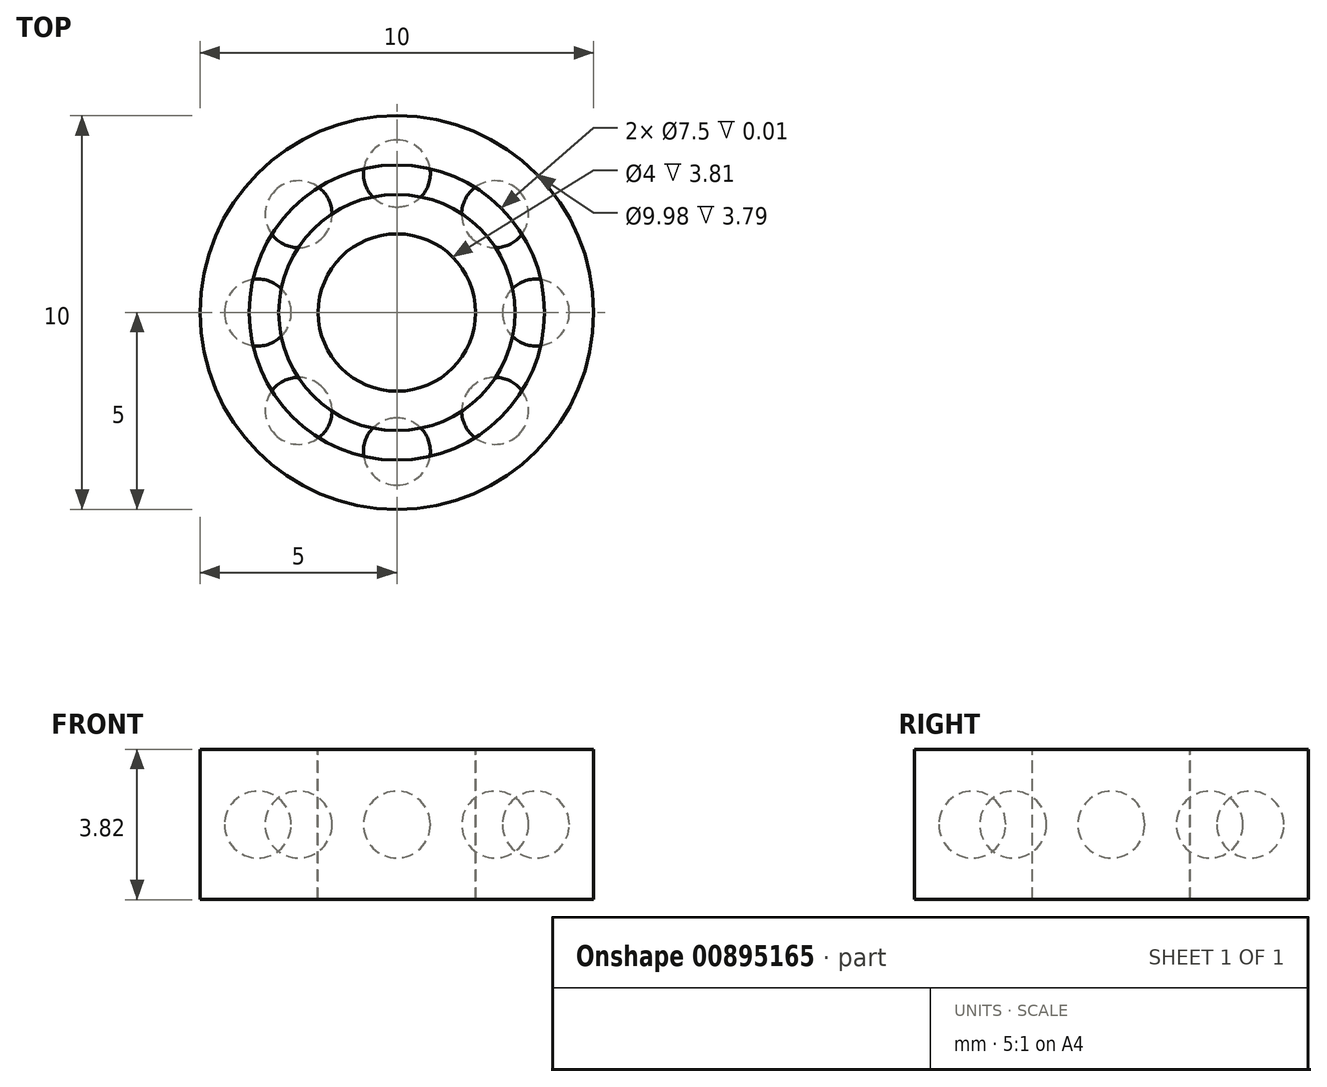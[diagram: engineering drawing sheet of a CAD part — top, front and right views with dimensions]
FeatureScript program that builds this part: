
annotation { "Feature Type Name" : "Feature", "Feature Type Description" : "" }
export const myFeature = defineFeature(function(context is Context, id is Id, definition is map)
    precondition{}
    {
        {
            var Q0;
            Q0=qCreatedBy(makeId("Top.planeOp"),FACE);
            var sketch = newSketch(context, id + "F0", { "sketchPlane" : qUnion([Q0])});
            skCircle(sketch, "E0", {"center": v(0, 0) * mm, "radius": 5 * mm});
            skSolve(sketch);
        }
        {
            var Q0;
            Q0=makeQuery(id+"F0.imprint","IMPRINT",FACE,{"disambiguationData":[TD([[makeQuery(id+"F0.imprint","IMPRINT",EDGE,{"derivedFrom":sQuery(id+"F0.wireOp",EDGE,"E0")}),1.0]])]});
            extrude(context, id + "F1", {"entities" : qUnion([Q0]), "endBound" : BoundingType.SYMMETRIC, "depth" : 3.8 * mm, "offsetDistance" : 25.4 * mm});
        }
        {
            var Q0;
            Q0=makeQuery(id+"F1.opExtrude","CAP_FACE",FACE,{"disambiguationData":[OSD([sQuery(id+"F0.wireOp",EDGE,"E0")])],"isStart":false});
            var sketch = newSketch(context, id + "F2", { "sketchPlane" : qUnion([Q0])});
            skCircle(sketch, "E1", {"center": v(0, 0) * mm, "radius": 2 * mm});
            skSolve(sketch);
        }
        {
            var Q0;
            Q0 = qSketchRegion(id + "F2", true);
            extrude(context, id + "F3", {"entities" : qUnion([Q0]), "operationType" : NewBodyOperationType.REMOVE, "endBound" : BoundingType.SYMMETRIC, "oppositeDirection" : true, "depth" : 25.4 * mm, "offsetDistance" : 25.4 * mm});
        }
        {
            var Q0;
            Q0=makeQuery(id+"F1.opExtrude","CAP_FACE",FACE,{"disambiguationData":[OSD([sQuery(id+"F0.wireOp",EDGE,"E0")])],"isStart":false});
            var sketch = newSketch(context, id + "F4", { "sketchPlane" : qUnion([Q0])});
            skCircle(sketch, "E2", {"center": v(0, 0) * mm, "radius": 3 * mm});
            skCircle(sketch, "E3", {"center": v(0, 0) * mm, "radius": 3.75 * mm});
            skSolve(sketch);
        }
        {
            var Q0;
            Q0=makeQuery(id+"F4.imprint","IMPRINT",FACE,{"disambiguationData":[TD([[makeQuery(id+"F4.imprint","IMPRINT",EDGE,{"derivedFrom":sQuery(id+"F4.wireOp",EDGE,"E2")}),-1.0]])]});
            extrude(context, id + "F5", {"entities" : qUnion([Q0]), "operationType" : NewBodyOperationType.REMOVE, "oppositeDirection" : true, "depth" : 25 * mm, "offsetDistance" : 25 * mm});
        }
        {
            var Q0;
            Q0=makeQuery(id+"F5.boolean.opBoolean","COPY",FACE,{"derivedFrom":makeQuery(id+"F5.opExtrude","SWEPT_FACE",FACE,{"disambiguationData":[OSD([sQuery(id+"F4.wireOp",EDGE,"E2")])]})});
            shell(context, id + "F6", {"entities" : qUnion([Q0]), "thickness" : 0.01 * mm});
        }
        {
            var Q0;
            Q0=makeQuery(id+"F5.boolean.opBoolean","COPY",FACE,{"derivedFrom":makeQuery(id+"F5.opExtrude","SWEPT_FACE",FACE,{"disambiguationData":[OSD([sQuery(id+"F4.wireOp",EDGE,"E3")])]})});
            shell(context, id + "F7", {"entities" : qUnion([Q0]), "thickness" : 0.01 * mm});
        }
        {
            var Q0;
            Q0=qCreatedBy(makeId("Top.planeOp"),FACE);
            var sketch = newSketch(context, id + "F8", { "sketchPlane" : qUnion([Q0])});
            skCircle(sketch, "E4", {"center": v(3.53, 0) * mm, "radius": 0.85 * mm});
            skLineSegment(sketch, "E5", {"start": v(4.38, 0) * mm, "end": v(2.68, 0) * mm});
            skSolve(sketch);
        }
        {
            var Q0;
            {var subQ0=sQuery(id+"F8.wireOp",EDGE,"E5");Q0=makeQuery(id+"F8.imprint","IMPRINT",FACE,{"disambiguationData":[TD([[makeQuery(id+"F8.imprint","IMPRINT",EDGE,{"derivedFrom":subQ0}),1.0]])]});}
            var Q1;
            Q1=sQuery(id+"F8.wireOp",EDGE,"E5");
            revolve(context, id + "F9", {"surfaceOperationType" : NewSurfaceOperationType.NEW, "entities" : qUnion([Q0]), "axis" : qUnion([Q1]), "revolveType" : RevolveType.FULL});
        }
        {
            var Q0;
            Q0=makeQuery(id+"F9.opRevolve","SWEPT_BODY",BODY,{"disambiguationData":[OSD([sQuery(id+"F8.wireOp",EDGE,"E4"),sQuery(id+"F8.wireOp",EDGE,"E5")])]});
            var Q1;
            Q1=makeQuery(id+"F5.boolean.opBoolean","COPY",EDGE,{"derivedFrom":makeQuery(id+"F5.opExtrude","CAP_EDGE",EDGE,{"disambiguationData":[OSD([sQuery(id+"F4.wireOp",EDGE,"E2")])],"isStart":true})});
            circularPattern(context, id + "F10", {"entities" : qUnion([Q0]), "axis" : qUnion([Q1]), "angle" : 360 * degree, "instanceCount" : 8, "equalSpace" : true});
        }
    });
